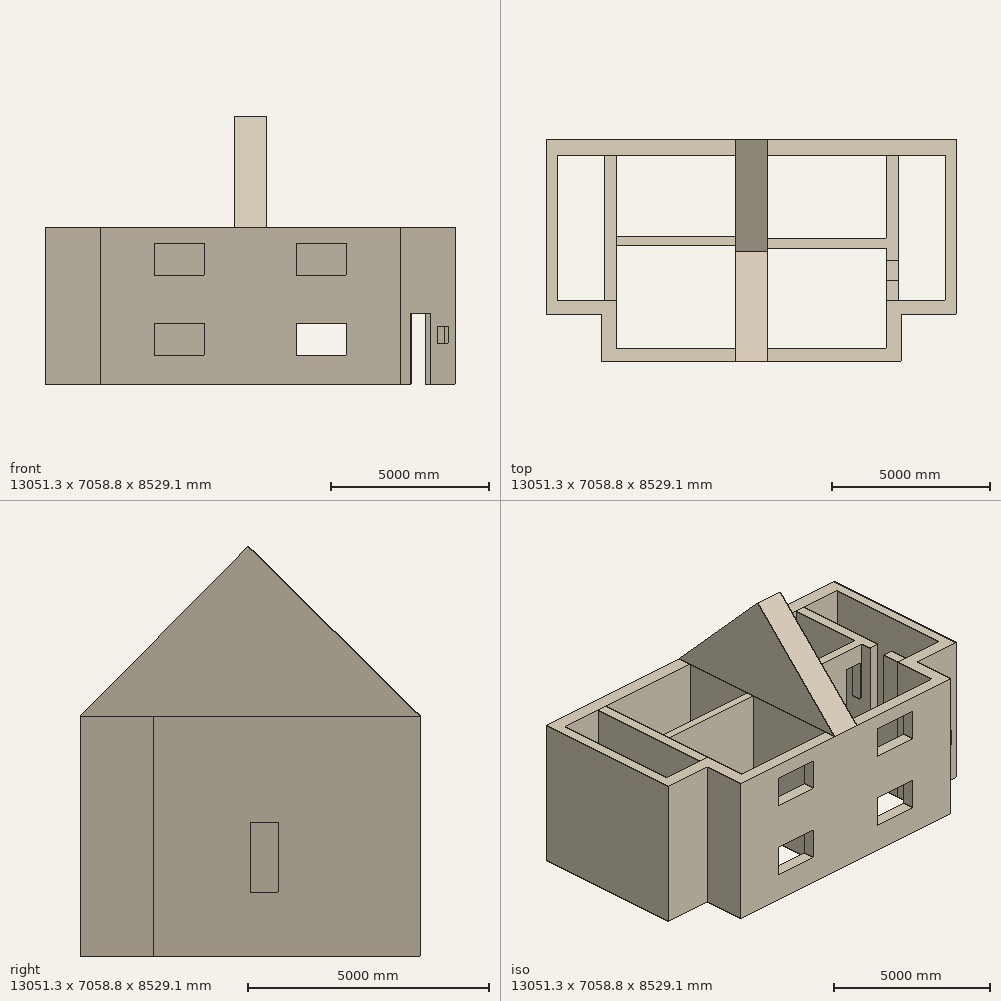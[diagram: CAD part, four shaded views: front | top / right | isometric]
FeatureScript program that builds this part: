
annotation { "Feature Type Name" : "Feature", "Feature Type Description" : "" }
export const myFeature = defineFeature(function(context is Context, id is Id, definition is map)
    precondition{}
    {
        {
            var Q0;
            Q0=qCreatedBy(makeId("Top.planeOp"),FACE);
            var sketch = newSketch(context, id + "F0", { "sketchPlane" : qUnion([Q0])});
            skLineSegment(sketch, "E0", {"start": v(0, 0) * mm, "end": v(4759.33, 0) * mm});
            skLineSegment(sketch, "E1", {"start": v(4759.33, 0) * mm, "end": v(4759.33, 1502.17) * mm});
            skLineSegment(sketch, "E2", {"start": v(4759.33, 1502.17) * mm, "end": v(6525.64, 1502.17) * mm});
            skLineSegment(sketch, "E3", {"start": v(6525.64, 1502.17) * mm, "end": v(6525.64, 7058.82) * mm});
            skLineSegment(sketch, "E4", {"start": v(6525.64, 7058.82) * mm, "end": v(0, 7058.82) * mm});
            skLineSegment(sketch, "E5", {"start": v(0, 6563.8) * mm, "end": v(6169.43, 6563.8) * mm});
            skLineSegment(sketch, "E6", {"start": v(6169.43, 6563.8) * mm, "end": v(6169.43, 1947.26) * mm});
            skLineSegment(sketch, "E7", {"start": v(6169.43, 1947.26) * mm, "end": v(4307.74, 1947.26) * mm});
            skLineSegment(sketch, "E8", {"start": v(0, 0) * mm, "end": v(0, 8027.33) * mm, "construction": true});
            skLineSegment(sketch, "E9", {"start": v(4307.74, 1947.26) * mm, "end": v(4307.74, 408.4) * mm});
            skLineSegment(sketch, "E10", {"start": v(4307.74, 408.4) * mm, "end": v(0, 408.4) * mm});
            skLineSegment(sketch, "E11.MirrorCS", {"start": v(-4307.74, 408.4) * mm, "end": v(0, 408.4) * mm});
            skLineSegment(sketch, "E12.MirrorCS", {"start": v(0, 0) * mm, "end": v(-4759.33, 0) * mm});
            skLineSegment(sketch, "E13.MirrorCS", {"start": v(-4759.33, 0) * mm, "end": v(-4759.33, 1502.17) * mm});
            skLineSegment(sketch, "E14.MirrorCS", {"start": v(-4307.74, 1947.26) * mm, "end": v(-4307.74, 408.4) * mm});
            skLineSegment(sketch, "E15.MirrorCS", {"start": v(-4759.33, 1502.17) * mm, "end": v(-6525.64, 1502.17) * mm});
            skLineSegment(sketch, "E16.MirrorCS", {"start": v(-6169.43, 1947.26) * mm, "end": v(-4307.74, 1947.26) * mm});
            skLineSegment(sketch, "E17.MirrorCS", {"start": v(-6525.64, 1502.17) * mm, "end": v(-6525.64, 7058.82) * mm});
            skLineSegment(sketch, "E18.MirrorCS", {"start": v(-6169.43, 6563.8) * mm, "end": v(-6169.43, 1947.26) * mm});
            skLineSegment(sketch, "E19.MirrorCS", {"start": v(-6525.64, 7058.82) * mm, "end": v(0, 7058.82) * mm});
            skLineSegment(sketch, "E20.MirrorCS", {"start": v(0, 6563.8) * mm, "end": v(-6169.43, 6563.8) * mm});
            skSolve(sketch);
        }
        {
            var Q0;
            Q0=makeQuery(id+"F0.imprint","IMPRINT",FACE,{"disambiguationData":[TD([[makeQuery(id+"F0.imprint","IMPRINT",EDGE,{"derivedFrom":sQuery(id+"F0.wireOp",EDGE,"E0")}),1.0]])]});
            extrude(context, id + "F1", {"entities" : qUnion([Q0]), "depth" : 5000 * mm, "offsetDistance" : 25 * mm});
        }
        {
            var Q0;
            Q0=makeQuery(id+"F1.opExtrude","CAP_FACE",FACE,{"disambiguationData":[OSD([sQuery(id+"F0.wireOp",EDGE,"E0"),sQuery(id+"F0.wireOp",EDGE,"E1"),sQuery(id+"F0.wireOp",EDGE,"E2"),sQuery(id+"F0.wireOp",EDGE,"E3"),sQuery(id+"F0.wireOp",EDGE,"E4"),sQuery(id+"F0.wireOp",EDGE,"E5"),sQuery(id+"F0.wireOp",EDGE,"E6"),sQuery(id+"F0.wireOp",EDGE,"E7"),sQuery(id+"F0.wireOp",EDGE,"E9"),sQuery(id+"F0.wireOp",EDGE,"E10"),sQuery(id+"F0.wireOp",EDGE,"E11.MirrorCS"),sQuery(id+"F0.wireOp",EDGE,"E12.MirrorCS"),sQuery(id+"F0.wireOp",EDGE,"E13.MirrorCS"),sQuery(id+"F0.wireOp",EDGE,"E14.MirrorCS"),sQuery(id+"F0.wireOp",EDGE,"E15.MirrorCS"),sQuery(id+"F0.wireOp",EDGE,"E16.MirrorCS"),sQuery(id+"F0.wireOp",EDGE,"E17.MirrorCS"),sQuery(id+"F0.wireOp",EDGE,"E18.MirrorCS"),sQuery(id+"F0.wireOp",EDGE,"E19.MirrorCS"),sQuery(id+"F0.wireOp",EDGE,"E20.MirrorCS")])],"isStart":true});
            var sketch = newSketch(context, id + "F2", { "sketchPlane" : qUnion([Q0])});
            skLineSegment(sketch, "E21.bottom", {"start": v(505.5, -408.4) * mm, "end": v(-505.5, -408.4) * mm});
            skLineSegment(sketch, "E21.top", {"start": v(505.5, -6563.8) * mm, "end": v(-505.5, -6563.8) * mm});
            skLineSegment(sketch, "E21.left", {"start": v(505.5, -408.4) * mm, "end": v(505.5, -6563.8) * mm});
            skLineSegment(sketch, "E21.right", {"start": v(-505.5, -408.4) * mm, "end": v(-505.5, -6563.8) * mm});
            skPoint(sketch, "E21.middle", {"position": v(0, -3486.1) * mm});
            skLineSegment(sketch, "E22.bottom", {"start": v(4666.04, -1947.26) * mm, "end": v(4307.74, -1947.26) * mm});
            skLineSegment(sketch, "E22.top", {"start": v(4666.04, -6563.8) * mm, "end": v(4307.74, -6563.8) * mm});
            skLineSegment(sketch, "E22.left", {"start": v(4666.04, -1947.26) * mm, "end": v(4666.04, -6563.8) * mm});
            skLineSegment(sketch, "E22.right", {"start": v(4307.74, -1947.26) * mm, "end": v(4307.74, -6563.8) * mm});
            skPoint(sketch, "E22.middle", {"position": v(4486.9, -4255.53) * mm});
            skLineSegment(sketch, "E23", {"start": v(0, 0) * mm, "end": v(0, -9806.48) * mm, "construction": true});
            skLineSegment(sketch, "E24.MirrorCS", {"start": v(-4307.74, -1947.26) * mm, "end": v(-4307.74, -6563.8) * mm});
            skLineSegment(sketch, "E25.MirrorCS", {"start": v(-4666.04, -6563.8) * mm, "end": v(-4307.74, -6563.8) * mm});
            skPoint(sketch, "E26.MirrorP", {"position": v(-4486.9, -4255.53) * mm});
            skLineSegment(sketch, "E27.MirrorCS", {"start": v(-4666.04, -1947.26) * mm, "end": v(-4307.74, -1947.26) * mm});
            skLineSegment(sketch, "E28.MirrorCS", {"start": v(-4666.04, -1947.26) * mm, "end": v(-4666.04, -6563.8) * mm});
            skSolve(sketch);
        }
        {
            var Q0;
            Q0=makeQuery(id+"F2.imprint","IMPRINT",FACE,{"disambiguationData":[TD([[makeQuery(id+"F2.imprint","IMPRINT",EDGE,{"derivedFrom":sQuery(id+"F2.wireOp",EDGE,"E24.MirrorCS")}),-1.0]])]});
            var Q1;
            Q1=makeQuery(id+"F2.imprint","IMPRINT",FACE,{"disambiguationData":[TD([[makeQuery(id+"F2.imprint","IMPRINT",EDGE,{"derivedFrom":sQuery(id+"F2.wireOp",EDGE,"E21.bottom")}),1.0]])]});
            var Q2;
            Q2=makeQuery(id+"F2.imprint","IMPRINT",FACE,{"disambiguationData":[TD([[makeQuery(id+"F2.imprint","IMPRINT",EDGE,{"derivedFrom":sQuery(id+"F2.wireOp",EDGE,"E22.bottom")}),1.0]])]});
            var Q3;
            Q3=makeQuery(id+"F1.opExtrude","CAP_FACE",FACE,{"disambiguationData":[OSD([sQuery(id+"F0.wireOp",EDGE,"E0"),sQuery(id+"F0.wireOp",EDGE,"E1"),sQuery(id+"F0.wireOp",EDGE,"E2"),sQuery(id+"F0.wireOp",EDGE,"E3"),sQuery(id+"F0.wireOp",EDGE,"E4"),sQuery(id+"F0.wireOp",EDGE,"E5"),sQuery(id+"F0.wireOp",EDGE,"E6"),sQuery(id+"F0.wireOp",EDGE,"E7"),sQuery(id+"F0.wireOp",EDGE,"E9"),sQuery(id+"F0.wireOp",EDGE,"E10"),sQuery(id+"F0.wireOp",EDGE,"E11.MirrorCS"),sQuery(id+"F0.wireOp",EDGE,"E12.MirrorCS"),sQuery(id+"F0.wireOp",EDGE,"E13.MirrorCS"),sQuery(id+"F0.wireOp",EDGE,"E14.MirrorCS"),sQuery(id+"F0.wireOp",EDGE,"E15.MirrorCS"),sQuery(id+"F0.wireOp",EDGE,"E16.MirrorCS"),sQuery(id+"F0.wireOp",EDGE,"E17.MirrorCS"),sQuery(id+"F0.wireOp",EDGE,"E18.MirrorCS"),sQuery(id+"F0.wireOp",EDGE,"E19.MirrorCS"),sQuery(id+"F0.wireOp",EDGE,"E20.MirrorCS")])],"isStart":false});
            extrude(context, id + "F3", {"entities" : qUnion([Q0, Q1, Q2]), "endBound" : BoundingType.UP_TO_SURFACE, "oppositeDirection" : true, "depth" : 25 * mm, "endBoundEntityFace" : qUnion([Q3]), "offsetDistance" : 25 * mm});
        }
        {
            var Q0;
            Q0=makeQuery(id+"F1.opExtrude","SWEPT_FACE",FACE,{"disambiguationData":[OSD([sQuery(id+"F0.wireOp",EDGE,"E5"),sQuery(id+"F0.wireOp",EDGE,"E20.MirrorCS")])]});
            var sketch = newSketch(context, id + "F4", { "sketchPlane" : qUnion([Q0])});
            skLineSegment(sketch, "E29.bottom", {"start": v(4962.62, 0) * mm, "end": v(5560.63, 0) * mm});
            skLineSegment(sketch, "E29.top", {"start": v(4962.62, 2378.31) * mm, "end": v(5560.63, 2378.31) * mm});
            skLineSegment(sketch, "E29.left", {"start": v(4962.62, 0) * mm, "end": v(4962.62, 2378.31) * mm});
            skLineSegment(sketch, "E29.right", {"start": v(5560.63, 0) * mm, "end": v(5560.63, 2378.31) * mm});
            skLineSegment(sketch, "E30", {"start": v(0, -12071.4) * mm, "end": v(0, 10012.17) * mm, "construction": true});
            skLineSegment(sketch, "E31.MirrorCS", {"start": v(-5560.63, 0) * mm, "end": v(-5560.63, 2378.31) * mm});
            skLineSegment(sketch, "E32.MirrorCS", {"start": v(-4962.62, 0) * mm, "end": v(-5560.63, 0) * mm});
            skLineSegment(sketch, "E33.MirrorCS", {"start": v(-4962.62, 2378.31) * mm, "end": v(-5560.63, 2378.31) * mm});
            skLineSegment(sketch, "E34.MirrorCS", {"start": v(-4962.62, 0) * mm, "end": v(-4962.62, 2378.31) * mm});
            skSolve(sketch);
        }
        {
            var Q0;
            Q0=makeQuery(id+"F4.imprint","IMPRINT",FACE,{"disambiguationData":[TD([[makeQuery(id+"F4.imprint","IMPRINT",EDGE,{"derivedFrom":sQuery(id+"F4.wireOp",EDGE,"E31.MirrorCS")}),-1.0]])]});
            var Q1;
            Q1=makeQuery(id+"F4.imprint","IMPRINT",FACE,{"disambiguationData":[TD([[makeQuery(id+"F4.imprint","IMPRINT",EDGE,{"derivedFrom":sQuery(id+"F4.wireOp",EDGE,"E29.bottom")}),-1.0]])]});
            extrude(context, id + "F5", {"entities" : qUnion([Q0, Q1]), "operationType" : NewBodyOperationType.REMOVE, "endBound" : BoundingType.THROUGH_ALL, "oppositeDirection" : true, "depth" : 25 * mm, "offsetDistance" : 25 * mm});
        }
        {
            var Q0;
            Q0=makeQuery(id+"F3.opExtrude","SWEPT_FACE",FACE,{"disambiguationData":[OSD([sQuery(id+"F2.wireOp",EDGE,"E28.MirrorCS")])]});
            var sketch = newSketch(context, id + "F6", { "sketchPlane" : qUnion([Q0])});
            skLineSegment(sketch, "E35.bottom", {"start": v(-5479.93, 0) * mm, "end": v(-4565.75, 0) * mm});
            skLineSegment(sketch, "E35.top", {"start": v(-5479.93, 1721.05) * mm, "end": v(-4565.75, 1721.05) * mm});
            skLineSegment(sketch, "E35.left", {"start": v(-5479.93, 0) * mm, "end": v(-5479.93, 1721.05) * mm});
            skLineSegment(sketch, "E35.right", {"start": v(-4565.75, 0) * mm, "end": v(-4565.75, 1721.05) * mm});
            skSolve(sketch);
        }
        {
            var Q0;
            Q0=makeQuery(id+"F6.imprint","IMPRINT",FACE,{"disambiguationData":[TD([[makeQuery(id+"F6.imprint","IMPRINT",EDGE,{"derivedFrom":sQuery(id+"F6.wireOp",EDGE,"E35.bottom")}),-1.0]])]});
            var Q1;
            Q1=makeQuery(id+"F3.opExtrude","SWEPT_FACE",FACE,{"disambiguationData":[OSD([sQuery(id+"F2.wireOp",EDGE,"E22.left")])]});
            extrude(context, id + "F7", {"entities" : qUnion([Q0]), "operationType" : NewBodyOperationType.REMOVE, "endBound" : BoundingType.UP_TO_SURFACE, "oppositeDirection" : true, "depth" : 25 * mm, "endBoundEntityFace" : qUnion([Q1]), "offsetDistance" : 25 * mm});
        }
        {
            var Q0;
            {var subQ0=sQuery(id+"F0.wireOp",EDGE,"E11.MirrorCS");var subQ1=sQuery(id+"F0.wireOp",EDGE,"E10");var subQ2=sQuery(id+"F0.wireOp",EDGE,"E9");var subQ3=sQuery(id+"F0.wireOp",EDGE,"E7");var subQ4=sQuery(id+"F0.wireOp",EDGE,"E6");var subQ5=sQuery(id+"F0.wireOp",EDGE,"E20.MirrorCS");var subQ6=sQuery(id+"F0.wireOp",EDGE,"E5");var subQ7=sQuery(id+"F0.wireOp",EDGE,"E19.MirrorCS");var subQ8=sQuery(id+"F0.wireOp",EDGE,"E4");var subQ9=sQuery(id+"F0.wireOp",EDGE,"E12.MirrorCS");var subQ10=sQuery(id+"F0.wireOp",EDGE,"E0");var subQ11=sQuery(id+"F0.wireOp",EDGE,"E1");var subQ12=sQuery(id+"F0.wireOp",EDGE,"E2");var subQ13=sQuery(id+"F0.wireOp",EDGE,"E3");var subQ14=sQuery(id+"F0.wireOp",EDGE,"E13.MirrorCS");var subQ15=sQuery(id+"F0.wireOp",EDGE,"E14.MirrorCS");var subQ16=sQuery(id+"F0.wireOp",EDGE,"E15.MirrorCS");var subQ17=sQuery(id+"F0.wireOp",EDGE,"E16.MirrorCS");var subQ18=sQuery(id+"F0.wireOp",EDGE,"E17.MirrorCS");var subQ19=sQuery(id+"F0.wireOp",EDGE,"E18.MirrorCS");Q0=makeQuery(id+"F5.boolean.opBoolean","SPLIT",FACE,{"disambiguationData":[TD([makeQuery(id+"F1.opExtrude","SWEPT_FACE",FACE,{"disambiguationData":[OSD([subQ11])]})])],"derivedFrom":makeQuery(id+"F1.opExtrude","CAP_FACE",FACE,{"disambiguationData":[OSD([subQ10,subQ11,subQ12,subQ13,subQ8,subQ6,subQ4,subQ3,subQ2,subQ1,subQ0,subQ9,subQ14,subQ15,subQ16,subQ17,subQ18,subQ19,subQ7,subQ5])],"isStart":true})});}
            var sketch = newSketch(context, id + "F8", { "sketchPlane" : qUnion([Q0])});
            skLineSegment(sketch, "E36.bottom", {"start": v(-4307.74, -3966.42) * mm, "end": v(-505.5, -3966.42) * mm});
            skLineSegment(sketch, "E36.top", {"start": v(-4307.74, -3702.56) * mm, "end": v(-505.5, -3702.56) * mm});
            skLineSegment(sketch, "E36.left", {"start": v(-4307.74, -3966.42) * mm, "end": v(-4307.74, -3702.56) * mm});
            skLineSegment(sketch, "E36.right", {"start": v(-505.5, -3966.42) * mm, "end": v(-505.5, -3702.56) * mm});
            skSolve(sketch);
        }
        {
            var Q0;
            Q0=makeQuery(id+"F8.imprint","IMPRINT",FACE,{"disambiguationData":[TD([[makeQuery(id+"F8.imprint","IMPRINT",EDGE,{"derivedFrom":sQuery(id+"F8.wireOp",EDGE,"E36.bottom")}),1.0]])]});
            var Q1;
            Q1=makeQuery(id+"F3.opExtrude","CAP_FACE",FACE,{"disambiguationData":[OSD([sQuery(id+"F2.wireOp",EDGE,"E21.bottom"),sQuery(id+"F2.wireOp",EDGE,"E21.top"),sQuery(id+"F2.wireOp",EDGE,"E21.left"),sQuery(id+"F2.wireOp",EDGE,"E21.right")])],"isStart":false});
            extrude(context, id + "F9", {"entities" : qUnion([Q0]), "endBound" : BoundingType.UP_TO_SURFACE, "oppositeDirection" : true, "depth" : 25 * mm, "endBoundEntityFace" : qUnion([Q1]), "offsetDistance" : 25 * mm});
        }
        {
            var Q0;
            Q0=makeQuery(id+"F1.opExtrude","SWEPT_FACE",FACE,{"disambiguationData":[OSD([sQuery(id+"F0.wireOp",EDGE,"E0"),sQuery(id+"F0.wireOp",EDGE,"E12.MirrorCS")])]});
            var sketch = newSketch(context, id + "F10", { "sketchPlane" : qUnion([Q0])});
            skLineSegment(sketch, "E37.bottom", {"start": v(1458.92, 1936.75) * mm, "end": v(3048.73, 1936.75) * mm});
            skLineSegment(sketch, "E37.top", {"start": v(1458.92, 921.06) * mm, "end": v(3048.73, 921.06) * mm});
            skLineSegment(sketch, "E37.left", {"start": v(1458.92, 1936.75) * mm, "end": v(1458.92, 921.06) * mm});
            skLineSegment(sketch, "E37.right", {"start": v(3048.73, 1936.75) * mm, "end": v(3048.73, 921.06) * mm});
            skLineSegment(sketch, "E38.bottom", {"start": v(1458.92, 4492.93) * mm, "end": v(3048.73, 4492.93) * mm});
            skLineSegment(sketch, "E38.top", {"start": v(1458.92, 3481.13) * mm, "end": v(3048.73, 3481.13) * mm});
            skLineSegment(sketch, "E38.left", {"start": v(1458.92, 4492.93) * mm, "end": v(1458.92, 3481.13) * mm});
            skLineSegment(sketch, "E38.right", {"start": v(3048.73, 4492.93) * mm, "end": v(3048.73, 3481.13) * mm});
            skLineSegment(sketch, "E39", {"start": v(0, 0) * mm, "end": v(0, 10373.43) * mm, "construction": true});
            skLineSegment(sketch, "E40.MirrorCS", {"start": v(-1458.92, 1936.75) * mm, "end": v(-3048.73, 1936.75) * mm});
            skLineSegment(sketch, "E41.MirrorCS", {"start": v(-3048.73, 4492.93) * mm, "end": v(-3048.73, 3481.13) * mm});
            skLineSegment(sketch, "E42.MirrorCS", {"start": v(-1458.92, 921.06) * mm, "end": v(-3048.73, 921.06) * mm});
            skLineSegment(sketch, "E43.MirrorCS", {"start": v(-1458.92, 4492.93) * mm, "end": v(-1458.92, 3481.13) * mm});
            skLineSegment(sketch, "E44.MirrorCS", {"start": v(-1458.92, 1936.75) * mm, "end": v(-1458.92, 921.06) * mm});
            skLineSegment(sketch, "E45.MirrorCS", {"start": v(-1458.92, 4492.93) * mm, "end": v(-3048.73, 4492.93) * mm});
            skLineSegment(sketch, "E46.MirrorCS", {"start": v(-3048.73, 1936.75) * mm, "end": v(-3048.73, 921.06) * mm});
            skLineSegment(sketch, "E47.MirrorCS", {"start": v(-1458.92, 3481.13) * mm, "end": v(-3048.73, 3481.13) * mm});
            skSolve(sketch);
        }
        {
            var Q0;
            Q0=makeQuery(id+"F10.imprint","IMPRINT",FACE,{"disambiguationData":[TD([[makeQuery(id+"F10.imprint","IMPRINT",EDGE,{"derivedFrom":sQuery(id+"F10.wireOp",EDGE,"E41.MirrorCS")}),1.0]])]});
            var Q1;
            Q1=makeQuery(id+"F10.imprint","IMPRINT",FACE,{"disambiguationData":[TD([[makeQuery(id+"F10.imprint","IMPRINT",EDGE,{"derivedFrom":sQuery(id+"F10.wireOp",EDGE,"E40.MirrorCS")}),1.0]])]});
            var Q2;
            Q2=makeQuery(id+"F10.imprint","IMPRINT",FACE,{"disambiguationData":[TD([[makeQuery(id+"F10.imprint","IMPRINT",EDGE,{"derivedFrom":sQuery(id+"F10.wireOp",EDGE,"E38.bottom")}),-1.0]])]});
            var Q3;
            Q3=makeQuery(id+"F10.imprint","IMPRINT",FACE,{"disambiguationData":[TD([[makeQuery(id+"F10.imprint","IMPRINT",EDGE,{"derivedFrom":sQuery(id+"F10.wireOp",EDGE,"E37.bottom")}),-1.0]])]});
            extrude(context, id + "F11", {"entities" : qUnion([Q0, Q1, Q2, Q3]), "operationType" : NewBodyOperationType.REMOVE, "endBound" : BoundingType.UP_TO_NEXT, "oppositeDirection" : true, "depth" : 25 * mm, "offsetDistance" : 25 * mm});
        }
        {
            var Q0;
            Q0=makeQuery(id+"F1.opExtrude","SWEPT_FACE",FACE,{"disambiguationData":[OSD([sQuery(id+"F0.wireOp",EDGE,"E2")])]});
            var sketch = newSketch(context, id + "F12", { "sketchPlane" : qUnion([Q0])});
            skLineSegment(sketch, "E48.bottom", {"start": v(5109.05, 0) * mm, "end": v(5743.11, 0) * mm});
            skLineSegment(sketch, "E48.top", {"start": v(5109.05, 2262.34) * mm, "end": v(5743.11, 2262.34) * mm});
            skLineSegment(sketch, "E48.left", {"start": v(5109.05, 0) * mm, "end": v(5109.05, 2262.34) * mm});
            skLineSegment(sketch, "E48.right", {"start": v(5743.11, 0) * mm, "end": v(5743.11, 2262.34) * mm});
            skLineSegment(sketch, "E49.bottom", {"start": v(5954.81, 1850.45) * mm, "end": v(6292.73, 1850.45) * mm});
            skLineSegment(sketch, "E49.top", {"start": v(5954.81, 1292.14) * mm, "end": v(6292.73, 1292.14) * mm});
            skLineSegment(sketch, "E49.left", {"start": v(5954.81, 1850.45) * mm, "end": v(5954.81, 1292.14) * mm});
            skLineSegment(sketch, "E49.right", {"start": v(6292.73, 1850.45) * mm, "end": v(6292.73, 1292.14) * mm});
            skSolve(sketch);
        }
        {
            var Q0;
            Q0=makeQuery(id+"F12.imprint","IMPRINT",FACE,{"disambiguationData":[TD([[makeQuery(id+"F12.imprint","IMPRINT",EDGE,{"derivedFrom":sQuery(id+"F12.wireOp",EDGE,"E48.bottom")}),1.0]])]});
            var Q1;
            Q1=makeQuery(id+"F12.imprint","IMPRINT",FACE,{"disambiguationData":[TD([[makeQuery(id+"F12.imprint","IMPRINT",EDGE,{"derivedFrom":sQuery(id+"F12.wireOp",EDGE,"E49.bottom")}),-1.0]])]});
            var Q2;
            Q2=makeQuery(id+"F1.opExtrude","SWEPT_FACE",FACE,{"disambiguationData":[OSD([sQuery(id+"F0.wireOp",EDGE,"E7")])]});
            var Q3;
            Q3=makeQuery(id+"F1.opExtrude","SWEPT_BODY",BODY,{"disambiguationData":[OSD([sQuery(id+"F0.wireOp",EDGE,"E0"),sQuery(id+"F0.wireOp",EDGE,"E1"),sQuery(id+"F0.wireOp",EDGE,"E2"),sQuery(id+"F0.wireOp",EDGE,"E3"),sQuery(id+"F0.wireOp",EDGE,"E4"),sQuery(id+"F0.wireOp",EDGE,"E5"),sQuery(id+"F0.wireOp",EDGE,"E6"),sQuery(id+"F0.wireOp",EDGE,"E7"),sQuery(id+"F0.wireOp",EDGE,"E9"),sQuery(id+"F0.wireOp",EDGE,"E10"),sQuery(id+"F0.wireOp",EDGE,"E11.MirrorCS"),sQuery(id+"F0.wireOp",EDGE,"E12.MirrorCS"),sQuery(id+"F0.wireOp",EDGE,"E13.MirrorCS"),sQuery(id+"F0.wireOp",EDGE,"E14.MirrorCS"),sQuery(id+"F0.wireOp",EDGE,"E15.MirrorCS"),sQuery(id+"F0.wireOp",EDGE,"E16.MirrorCS"),sQuery(id+"F0.wireOp",EDGE,"E17.MirrorCS"),sQuery(id+"F0.wireOp",EDGE,"E18.MirrorCS"),sQuery(id+"F0.wireOp",EDGE,"E19.MirrorCS"),sQuery(id+"F0.wireOp",EDGE,"E20.MirrorCS")])]});
            extrude(context, id + "F13", {"entities" : qUnion([Q0, Q1]), "operationType" : NewBodyOperationType.REMOVE, "endBound" : BoundingType.UP_TO_SURFACE, "oppositeDirection" : true, "depth" : 25 * mm, "endBoundEntityFace" : qUnion([Q2]), "endBoundEntityBody" : qUnion([Q3]), "offsetDistance" : 25 * mm});
        }
        {
            var Q0;
            Q0=makeQuery(id+"F3.opExtrude","SWEPT_FACE",FACE,{"disambiguationData":[OSD([sQuery(id+"F2.wireOp",EDGE,"E21.left")])]});
            var sketch = newSketch(context, id + "F14", { "sketchPlane" : qUnion([Q0])});
            skLineSegment(sketch, "E50", {"start": v(0, 5000) * mm, "end": v(3486.1, 8529.15) * mm});
            skLineSegment(sketch, "E51", {"start": v(3486.1, 8529.15) * mm, "end": v(7058.82, 5000) * mm});
            skPoint(sketch, "E51.endSnap0", {"position": v(3486.1, 5000) * mm});
            skLineSegment(sketch, "E52", {"start": v(7058.82, 5000) * mm, "end": v(0, 5000) * mm});
            skLineSegment(sketch, "E53", {"start": v(3486.1, 5000) * mm, "end": v(3486.1, 10804.5) * mm, "construction": true});
            skSolve(sketch);
        }
        {
            var Q0;
            Q0 = qSketchRegion(id + "F14", true);
            var Q1;
            Q1=makeQuery(id+"F3.opExtrude","SWEPT_FACE",FACE,{"disambiguationData":[OSD([sQuery(id+"F2.wireOp",EDGE,"E21.right")])]});
            extrude(context, id + "F15", {"entities" : qUnion([Q0]), "endBound" : BoundingType.UP_TO_SURFACE, "oppositeDirection" : true, "depth" : 25 * mm, "endBoundEntityFace" : qUnion([Q1]), "offsetDistance" : 25 * mm});
        }
        {
            var Q0;
            Q0=makeQuery(id+"F3.opExtrude","SWEPT_FACE",FACE,{"disambiguationData":[OSD([sQuery(id+"F2.wireOp",EDGE,"E22.left")])]});
            var sketch = newSketch(context, id + "F16", { "sketchPlane" : qUnion([Q0])});
            skLineSegment(sketch, "E54.bottom", {"start": v(4055.16, 0) * mm, "end": v(5094.13, 0) * mm});
            skLineSegment(sketch, "E54.top", {"start": v(4055.16, 2861.86) * mm, "end": v(5094.13, 2861.86) * mm});
            skLineSegment(sketch, "E54.left", {"start": v(4055.16, 0) * mm, "end": v(4055.16, 2861.86) * mm});
            skLineSegment(sketch, "E54.right", {"start": v(5094.13, 0) * mm, "end": v(5094.13, 2861.86) * mm});
            skSolve(sketch);
        }
        {
            var Q0;
            Q0=makeQuery(id+"F16.imprint","IMPRINT",FACE,{"disambiguationData":[TD([[makeQuery(id+"F16.imprint","IMPRINT",EDGE,{"derivedFrom":sQuery(id+"F16.wireOp",EDGE,"E54.bottom")}),1.0]])]});
            var Q1;
            Q1=makeQuery(id+"F3.opExtrude","SWEPT_FACE",FACE,{"disambiguationData":[OSD([sQuery(id+"F2.wireOp",EDGE,"E22.right")])]});
            extrude(context, id + "F17", {"entities" : qUnion([Q0]), "operationType" : NewBodyOperationType.REMOVE, "endBound" : BoundingType.UP_TO_SURFACE, "oppositeDirection" : true, "depth" : 25 * mm, "endBoundEntityFace" : qUnion([Q1]), "offsetDistance" : 25 * mm});
        }
        {
            var Q0;
            Q0=makeQuery(id+"F1.opExtrude","CAP_FACE",FACE,{"disambiguationData":[OSD([sQuery(id+"F0.wireOp",EDGE,"E0"),sQuery(id+"F0.wireOp",EDGE,"E1"),sQuery(id+"F0.wireOp",EDGE,"E2"),sQuery(id+"F0.wireOp",EDGE,"E3"),sQuery(id+"F0.wireOp",EDGE,"E4"),sQuery(id+"F0.wireOp",EDGE,"E5"),sQuery(id+"F0.wireOp",EDGE,"E6"),sQuery(id+"F0.wireOp",EDGE,"E7"),sQuery(id+"F0.wireOp",EDGE,"E9"),sQuery(id+"F0.wireOp",EDGE,"E10"),sQuery(id+"F0.wireOp",EDGE,"E11.MirrorCS"),sQuery(id+"F0.wireOp",EDGE,"E12.MirrorCS"),sQuery(id+"F0.wireOp",EDGE,"E13.MirrorCS"),sQuery(id+"F0.wireOp",EDGE,"E14.MirrorCS"),sQuery(id+"F0.wireOp",EDGE,"E15.MirrorCS"),sQuery(id+"F0.wireOp",EDGE,"E16.MirrorCS"),sQuery(id+"F0.wireOp",EDGE,"E17.MirrorCS"),sQuery(id+"F0.wireOp",EDGE,"E18.MirrorCS"),sQuery(id+"F0.wireOp",EDGE,"E19.MirrorCS"),sQuery(id+"F0.wireOp",EDGE,"E20.MirrorCS")])],"isStart":false});
            var sketch = newSketch(context, id + "F18", { "sketchPlane" : qUnion([Q0])});
            skLineSegment(sketch, "E55.bottom", {"start": v(4322.95, 3903.83) * mm, "end": v(518.79, 3903.83) * mm});
            skLineSegment(sketch, "E55.top", {"start": v(4322.95, 3581.28) * mm, "end": v(518.79, 3581.28) * mm});
            skLineSegment(sketch, "E55.left", {"start": v(4322.95, 3903.83) * mm, "end": v(4322.95, 3581.28) * mm});
            skLineSegment(sketch, "E55.right", {"start": v(518.79, 3903.83) * mm, "end": v(518.79, 3581.28) * mm});
            skSolve(sketch);
        }
        {
            var Q0;
            Q0=makeQuery(id+"F18.imprint","IMPRINT",FACE,{"disambiguationData":[TD([[makeQuery(id+"F18.imprint","IMPRINT",EDGE,{"derivedFrom":sQuery(id+"F18.wireOp",EDGE,"E55.bottom")}),1.0]])]});
            extrude(context, id + "F19", {"entities" : qUnion([Q0]), "operationType" : NewBodyOperationType.ADD, "oppositeDirection" : true, "depth" : 2000 * mm, "offsetDistance" : 25 * mm});
        }
        {
            var Q0;
            Q0=makeQuery(id+"F1.opExtrude","SWEPT_FACE",FACE,{"disambiguationData":[OSD([sQuery(id+"F0.wireOp",EDGE,"E5"),sQuery(id+"F0.wireOp",EDGE,"E20.MirrorCS")])]});
            var sketch = newSketch(context, id + "F20", { "sketchPlane" : qUnion([Q0])});
            skLineSegment(sketch, "E56.0", {"start": v(1458.92, 3481.13) * mm, "end": v(3048.73, 3481.13) * mm});
            skLineSegment(sketch, "E56.1", {"start": v(3048.73, 4492.93) * mm, "end": v(3048.73, 3481.13) * mm});
            skLineSegment(sketch, "E56.2", {"start": v(1458.92, 4492.93) * mm, "end": v(3048.73, 4492.93) * mm});
            skLineSegment(sketch, "E56.3", {"start": v(1458.92, 4492.93) * mm, "end": v(1458.92, 3481.13) * mm});
            skLineSegment(sketch, "E57.0", {"start": v(1458.92, 921.06) * mm, "end": v(3048.73, 921.06) * mm});
            skLineSegment(sketch, "E57.1", {"start": v(3048.73, 1936.75) * mm, "end": v(3048.73, 921.06) * mm});
            skLineSegment(sketch, "E57.2", {"start": v(1458.92, 1936.75) * mm, "end": v(3048.73, 1936.75) * mm});
            skLineSegment(sketch, "E57.3", {"start": v(1458.92, 1936.75) * mm, "end": v(1458.92, 921.06) * mm});
            skSolve(sketch);
        }
        {
            var Q0;
            Q0=makeQuery(id+"F20.imprint","IMPRINT",FACE,{"disambiguationData":[TD([[makeQuery(id+"F20.imprint","IMPRINT",EDGE,{"derivedFrom":sQuery(id+"F20.wireOp",EDGE,"E56.0")}),1.0]])]});
            var Q1;
            Q1=makeQuery(id+"F20.imprint","IMPRINT",FACE,{"disambiguationData":[TD([[makeQuery(id+"F20.imprint","IMPRINT",EDGE,{"derivedFrom":sQuery(id+"F20.wireOp",EDGE,"E57.0")}),1.0]])]});
            var Q2;
            Q2=makeQuery(id+"F1.opExtrude","SWEPT_FACE",FACE,{"disambiguationData":[OSD([sQuery(id+"F0.wireOp",EDGE,"E4"),sQuery(id+"F0.wireOp",EDGE,"E19.MirrorCS")])]});
            extrude(context, id + "F21", {"entities" : qUnion([Q0, Q1]), "operationType" : NewBodyOperationType.REMOVE, "endBound" : BoundingType.UP_TO_SURFACE, "oppositeDirection" : true, "depth" : 25 * mm, "endBoundEntityFace" : qUnion([Q2]), "offsetDistance" : 25 * mm});
        }
        {
            var Q0;
            Q0=makeQuery(id+"F1.opExtrude","SWEPT_FACE",FACE,{"disambiguationData":[OSD([sQuery(id+"F0.wireOp",EDGE,"E3")])]});
            var sketch = newSketch(context, id + "F22", { "sketchPlane" : qUnion([Q0])});
            skLineSegment(sketch, "E58.bottom", {"start": v(3525.53, 2793.13) * mm, "end": v(4112.11, 2793.13) * mm});
            skLineSegment(sketch, "E58.top", {"start": v(3525.53, 1322.2) * mm, "end": v(4112.11, 1322.2) * mm});
            skLineSegment(sketch, "E58.left", {"start": v(3525.53, 2793.13) * mm, "end": v(3525.53, 1322.2) * mm});
            skLineSegment(sketch, "E58.right", {"start": v(4112.11, 2793.13) * mm, "end": v(4112.11, 1322.2) * mm});
            skSolve(sketch);
        }
        {
            var Q0;
            Q0=makeQuery(id+"F22.imprint","IMPRINT",FACE,{"disambiguationData":[TD([[makeQuery(id+"F22.imprint","IMPRINT",EDGE,{"derivedFrom":sQuery(id+"F22.wireOp",EDGE,"E58.bottom")}),-1.0]])]});
            var Q1;
            Q1=makeQuery(id+"F1.opExtrude","SWEPT_FACE",FACE,{"disambiguationData":[OSD([sQuery(id+"F0.wireOp",EDGE,"E6")])]});
            extrude(context, id + "F23", {"entities" : qUnion([Q0]), "operationType" : NewBodyOperationType.REMOVE, "endBound" : BoundingType.UP_TO_SURFACE, "oppositeDirection" : true, "depth" : 25 * mm, "endBoundEntityFace" : qUnion([Q1]), "offsetDistance" : 25 * mm});
        }
        {
            var Q0;
            Q0=makeQuery(id+"F3.opExtrude","SWEPT_FACE",FACE,{"disambiguationData":[OSD([sQuery(id+"F2.wireOp",EDGE,"E22.left")])]});
            var sketch = newSketch(context, id + "F24", { "sketchPlane" : qUnion([Q0])});
            skLineSegment(sketch, "E59.bottom", {"start": v(3206.82, 5000) * mm, "end": v(2575.82, 5000) * mm});
            skLineSegment(sketch, "E59.top", {"start": v(3206.82, 2469.9) * mm, "end": v(2575.82, 2469.9) * mm});
            skLineSegment(sketch, "E59.left", {"start": v(3206.82, 5000) * mm, "end": v(3206.82, 2469.9) * mm});
            skLineSegment(sketch, "E59.right", {"start": v(2575.82, 5000) * mm, "end": v(2575.82, 2469.9) * mm});
            skSolve(sketch);
        }
        {
            var Q0;
            Q0=makeQuery(id+"F24.imprint","IMPRINT",FACE,{"disambiguationData":[TD([[makeQuery(id+"F24.imprint","IMPRINT",EDGE,{"derivedFrom":sQuery(id+"F24.wireOp",EDGE,"E59.bottom")}),-1.0]])]});
            var Q1;
            Q1=makeQuery(id+"F3.opExtrude","SWEPT_FACE",FACE,{"disambiguationData":[OSD([sQuery(id+"F2.wireOp",EDGE,"E22.right")])]});
            extrude(context, id + "F25", {"entities" : qUnion([Q0]), "operationType" : NewBodyOperationType.REMOVE, "endBound" : BoundingType.UP_TO_SURFACE, "oppositeDirection" : true, "depth" : 25 * mm, "endBoundEntityFace" : qUnion([Q1]), "offsetDistance" : 25 * mm});
        }
        {
            var Q0;
            Q0=makeQuery(id+"F19.opExtrude","SWEPT_FACE",FACE,{"disambiguationData":[OSD([sQuery(id+"F18.wireOp",EDGE,"E55.top")])]});
            var sketch = newSketch(context, id + "F26", { "sketchPlane" : qUnion([Q0])});
            skLineSegment(sketch, "E60.bottom", {"start": v(3621.5, 3000) * mm, "end": v(4225.5, 3000) * mm});
            skLineSegment(sketch, "E60.top", {"start": v(3621.5, 4324.33) * mm, "end": v(4225.5, 4324.33) * mm});
            skLineSegment(sketch, "E60.left", {"start": v(3621.5, 3000) * mm, "end": v(3621.5, 4324.33) * mm});
            skLineSegment(sketch, "E60.right", {"start": v(4225.5, 3000) * mm, "end": v(4225.5, 4324.33) * mm});
            skSolve(sketch);
        }
        {
            var Q0;
            Q0=makeQuery(id+"F26.imprint","IMPRINT",FACE,{"disambiguationData":[TD([[makeQuery(id+"F26.imprint","IMPRINT",EDGE,{"derivedFrom":sQuery(id+"F26.wireOp",EDGE,"E60.bottom")}),-1.0]])]});
            var Q1;
            Q1=makeQuery(id+"F19.opExtrude","SWEPT_FACE",FACE,{"disambiguationData":[OSD([sQuery(id+"F18.wireOp",EDGE,"E55.bottom")])]});
            extrude(context, id + "F27", {"entities" : qUnion([Q0]), "operationType" : NewBodyOperationType.REMOVE, "endBound" : BoundingType.UP_TO_SURFACE, "oppositeDirection" : true, "depth" : 25 * mm, "endBoundEntityFace" : qUnion([Q1]), "offsetDistance" : 25 * mm});
        }
    });
